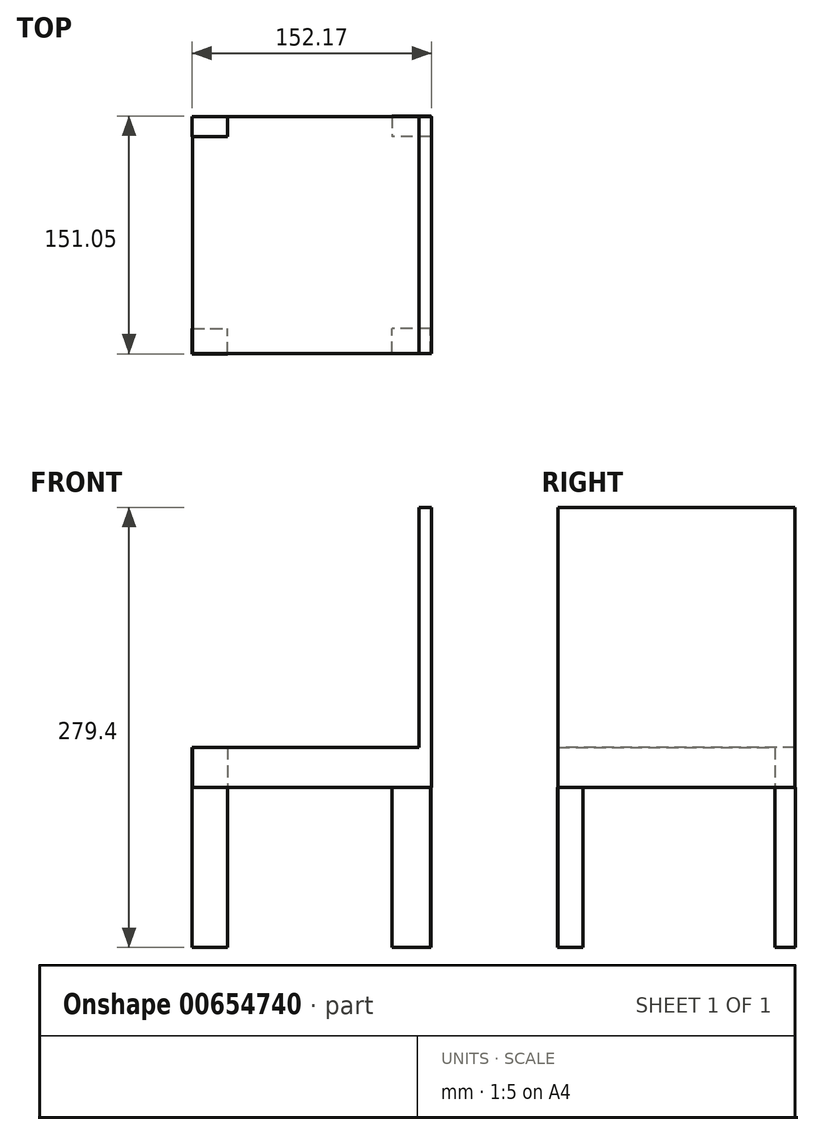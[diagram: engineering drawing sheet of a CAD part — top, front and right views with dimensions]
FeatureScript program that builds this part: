
annotation { "Feature Type Name" : "Feature", "Feature Type Description" : "" }
export const myFeature = defineFeature(function(context is Context, id is Id, definition is map)
    precondition{}
    {
        {
            var Q0;
            Q0=qCreatedBy(makeId("Top.planeOp"),FACE);
            var sketch = newSketch(context, id + "F0", { "sketchPlane" : qUnion([Q0])});
            skLineSegment(sketch, "E0.bottom", {"start": v(-76.1, -74.6) * mm, "end": v(-53.69, -74.6) * mm});
            skLineSegment(sketch, "E0.top", {"start": v(-76.1, -58.44) * mm, "end": v(-53.69, -58.44) * mm});
            skLineSegment(sketch, "E0.left", {"start": v(-76.1, -74.6) * mm, "end": v(-76.1, -58.44) * mm});
            skLineSegment(sketch, "E0.right", {"start": v(-53.69, -74.6) * mm, "end": v(-53.69, -58.44) * mm});
            skLineSegment(sketch, "E1.bottom", {"start": v(75.43, -74.27) * mm, "end": v(50.96, -74.27) * mm});
            skLineSegment(sketch, "E1.top", {"start": v(75.43, -58.44) * mm, "end": v(50.96, -58.44) * mm});
            skLineSegment(sketch, "E1.left", {"start": v(75.43, -74.27) * mm, "end": v(75.43, -58.44) * mm});
            skLineSegment(sketch, "E1.right", {"start": v(50.96, -74.27) * mm, "end": v(50.96, -58.44) * mm});
            skLineSegment(sketch, "E2.bottom", {"start": v(75.57, 76.45) * mm, "end": v(50.96, 76.45) * mm});
            skLineSegment(sketch, "E2.top", {"start": v(75.57, 63.39) * mm, "end": v(50.96, 63.39) * mm});
            skLineSegment(sketch, "E2.left", {"start": v(75.57, 76.45) * mm, "end": v(75.57, 63.39) * mm});
            skLineSegment(sketch, "E2.right", {"start": v(50.96, 76.45) * mm, "end": v(50.96, 63.39) * mm});
            skLineSegment(sketch, "E3.bottom", {"start": v(-75.96, 76.12) * mm, "end": v(-53.69, 76.12) * mm});
            skLineSegment(sketch, "E3.top", {"start": v(-75.96, 63.39) * mm, "end": v(-53.69, 63.39) * mm});
            skLineSegment(sketch, "E3.left", {"start": v(-75.96, 76.12) * mm, "end": v(-75.96, 63.39) * mm});
            skLineSegment(sketch, "E3.right", {"start": v(-53.69, 76.12) * mm, "end": v(-53.69, 63.39) * mm});
            skSolve(sketch);
        }
        {
            var Q0;
            Q0=makeQuery(id+"F0.imprint","IMPRINT",FACE,{"disambiguationData":[TD([[makeQuery(id+"F0.imprint","IMPRINT",EDGE,{"derivedFrom":sQuery(id+"F0.wireOp",EDGE,"E3.bottom")}),-1.0]])]});
            var Q1;
            Q1=makeQuery(id+"F0.imprint","IMPRINT",FACE,{"disambiguationData":[TD([[makeQuery(id+"F0.imprint","IMPRINT",EDGE,{"derivedFrom":sQuery(id+"F0.wireOp",EDGE,"E2.bottom")}),1.0]])]});
            var Q2;
            Q2=makeQuery(id+"F0.imprint","IMPRINT",FACE,{"disambiguationData":[TD([[makeQuery(id+"F0.imprint","IMPRINT",EDGE,{"derivedFrom":sQuery(id+"F0.wireOp",EDGE,"E1.bottom")}),-1.0]])]});
            var Q3;
            Q3=makeQuery(id+"F0.imprint","IMPRINT",FACE,{"disambiguationData":[TD([[makeQuery(id+"F0.imprint","IMPRINT",EDGE,{"derivedFrom":sQuery(id+"F0.wireOp",EDGE,"E0.bottom")}),1.0]])]});
            extrude(context, id + "F1", {"entities" : qUnion([Q0, Q1, Q2, Q3]), "depth" : 101.6 * mm, "offsetDistance" : 25.4 * mm});
        }
        {
            var Q0;
            Q0=makeQuery(id+"F1.opExtrude","CAP_FACE",FACE,{"disambiguationData":[OSD([sQuery(id+"F0.wireOp",EDGE,"E3.bottom"),sQuery(id+"F0.wireOp",EDGE,"E3.top"),sQuery(id+"F0.wireOp",EDGE,"E3.left"),sQuery(id+"F0.wireOp",EDGE,"E3.right")])],"isStart":false});
            var sketch = newSketch(context, id + "F2", { "sketchPlane" : qUnion([Q0])});
            skLineSegment(sketch, "E4.bottom", {"start": v(-75.77, -74.44) * mm, "end": v(76.07, -74.44) * mm});
            skLineSegment(sketch, "E4.top", {"start": v(-75.77, 76.2) * mm, "end": v(76.07, 76.2) * mm});
            skLineSegment(sketch, "E4.left", {"start": v(-75.77, -74.44) * mm, "end": v(-75.77, 76.2) * mm});
            skLineSegment(sketch, "E4.right", {"start": v(76.07, -74.44) * mm, "end": v(76.07, 76.2) * mm});
            skSolve(sketch);
        }
        {
            var Q0;
            {var subQ4=sQuery(id+"F2.wireOp",EDGE,"E4.bottom");Q0=makeQuery(id+"F2.imprint","IMPRINT",FACE,{"disambiguationData":[TD([[makeQuery(id+"F2.imprint","IMPRINT",EDGE,{"derivedFrom":subQ4}),1.0]])]});}
            extrude(context, id + "F3", {"entities" : qUnion([Q0]), "depth" : 25.4 * mm, "offsetDistance" : 25.4 * mm});
        }
        {
            var Q0;
            Q0=makeQuery(id+"F1.opExtrude","CAP_FACE",FACE,{"disambiguationData":[OSD([sQuery(id+"F0.wireOp",EDGE,"E3.bottom"),sQuery(id+"F0.wireOp",EDGE,"E3.top"),sQuery(id+"F0.wireOp",EDGE,"E3.left"),sQuery(id+"F0.wireOp",EDGE,"E3.right")])],"isStart":false});
            var sketch = newSketch(context, id + "F4", { "sketchPlane" : qUnion([Q0])});
            skLineSegment(sketch, "E5.bottom", {"start": v(-75.96, 76.12) * mm, "end": v(-53.69, 76.12) * mm});
            skLineSegment(sketch, "E5.top", {"start": v(-75.96, 63.39) * mm, "end": v(-53.69, 63.39) * mm});
            skLineSegment(sketch, "E5.left", {"start": v(-75.96, 76.12) * mm, "end": v(-75.96, 63.39) * mm});
            skLineSegment(sketch, "E5.right", {"start": v(-53.69, 76.12) * mm, "end": v(-53.69, 63.39) * mm});
            skSolve(sketch);
        }
        {
            var Q0;
            Q0=makeQuery(id+"F4.imprint","IMPRINT",FACE,{"disambiguationData":[TD([[makeQuery(id+"F4.imprint","IMPRINT",EDGE,{"derivedFrom":sQuery(id+"F4.wireOp",EDGE,"E5.bottom")}),-1.0]])]});
            extrude(context, id + "F5", {"entities" : qUnion([Q0]), "depth" : 25.4 * mm, "offsetDistance" : 25.4 * mm});
        }
        {
            var Q0;
            Q0=makeQuery(id+"F3.opExtrude","CAP_FACE",FACE,{"disambiguationData":[OSD([sQuery(id+"F0.wireOp",EDGE,"E3.bottom"),sQuery(id+"F0.wireOp",EDGE,"E3.top"),sQuery(id+"F0.wireOp",EDGE,"E3.right"),sQuery(id+"F2.wireOp",EDGE,"E4.bottom"),sQuery(id+"F2.wireOp",EDGE,"E4.top"),sQuery(id+"F2.wireOp",EDGE,"E4.left"),sQuery(id+"F2.wireOp",EDGE,"E4.right")])],"isStart":false});
            var sketch = newSketch(context, id + "F6", { "sketchPlane" : qUnion([Q0])});
            skLineSegment(sketch, "E6.bottom", {"start": v(76.07, 76.2) * mm, "end": v(67.94, 76.2) * mm});
            skLineSegment(sketch, "E6.top", {"start": v(76.07, -74.44) * mm, "end": v(67.94, -74.44) * mm});
            skLineSegment(sketch, "E6.left", {"start": v(76.07, 76.2) * mm, "end": v(76.07, -74.44) * mm});
            skLineSegment(sketch, "E6.right", {"start": v(67.94, 76.2) * mm, "end": v(67.94, -74.44) * mm});
            skSolve(sketch);
        }
        {
            var Q0;
            Q0=makeQuery(id+"F6.imprint","IMPRINT",FACE,{"disambiguationData":[TD([[makeQuery(id+"F6.imprint","IMPRINT",EDGE,{"derivedFrom":sQuery(id+"F6.wireOp",EDGE,"E6.bottom")}),-1.0]])]});
            extrude(context, id + "F7", {"entities" : qUnion([Q0]), "operationType" : NewBodyOperationType.ADD, "depth" : 76.2 * mm, "offsetDistance" : 25.4 * mm});
        }
        {
            var Q0;
            Q0=makeQuery(id+"F7.opExtrude","CAP_FACE",FACE,{"disambiguationData":[OSD([sQuery(id+"F6.wireOp",EDGE,"E6.bottom"),sQuery(id+"F6.wireOp",EDGE,"E6.top"),sQuery(id+"F6.wireOp",EDGE,"E6.left"),sQuery(id+"F6.wireOp",EDGE,"E6.right")])],"isStart":false});
            extrude(context, id + "F8", {"entities" : qUnion([Q0]), "operationType" : NewBodyOperationType.ADD, "depth" : 152.4 * mm, "offsetDistance" : 25.4 * mm});
        }
        {
            var Q0;
            Q0=makeQuery(id+"F8.opExtrude","CAP_FACE",FACE,{"disambiguationData":[OSD([sQuery(id+"F6.wireOp",EDGE,"E6.bottom"),sQuery(id+"F6.wireOp",EDGE,"E6.top"),sQuery(id+"F6.wireOp",EDGE,"E6.left"),sQuery(id+"F6.wireOp",EDGE,"E6.right")])],"isStart":false});
            extrude(context, id + "F9", {"entities" : qUnion([Q0]), "operationType" : NewBodyOperationType.ADD, "depth" : 127 * mm, "offsetDistance" : 25.4 * mm});
        }
        {
            var Q0;
            Q0=makeQuery(id+"F9.opExtrude","CAP_FACE",FACE,{"disambiguationData":[OSD([sQuery(id+"F6.wireOp",EDGE,"E6.bottom"),sQuery(id+"F6.wireOp",EDGE,"E6.top"),sQuery(id+"F6.wireOp",EDGE,"E6.left"),sQuery(id+"F6.wireOp",EDGE,"E6.right")])],"isStart":false});
            extrude(context, id + "F10", {"entities" : qUnion([Q0]), "operationType" : NewBodyOperationType.ADD, "depth" : 25.4 * mm, "offsetDistance" : 25.4 * mm});
        }
        {
            var Q0;
            Q0=makeQuery(id+"F10.opExtrude","CAP_FACE",FACE,{"disambiguationData":[OSD([sQuery(id+"F6.wireOp",EDGE,"E6.bottom"),sQuery(id+"F6.wireOp",EDGE,"E6.top"),sQuery(id+"F6.wireOp",EDGE,"E6.left"),sQuery(id+"F6.wireOp",EDGE,"E6.right")])],"isStart":false});
            extrude(context, id + "F11", {"entities" : qUnion([Q0]), "operationType" : NewBodyOperationType.REMOVE, "oppositeDirection" : true, "depth" : 76.2 * mm, "offsetDistance" : 25.4 * mm});
        }
        {
            var Q0;
            Q0=makeQuery(id+"F11.boolean.opBoolean","COPY",FACE,{"derivedFrom":makeQuery(id+"F11.opExtrude","CAP_FACE",FACE,{"disambiguationData":[OSD([sQuery(id+"F6.wireOp",EDGE,"E6.bottom"),sQuery(id+"F6.wireOp",EDGE,"E6.top"),sQuery(id+"F6.wireOp",EDGE,"E6.left"),sQuery(id+"F6.wireOp",EDGE,"E6.right")])],"isStart":false})});
            extrude(context, id + "F12", {"entities" : qUnion([Q0]), "operationType" : NewBodyOperationType.REMOVE, "oppositeDirection" : true, "depth" : 76.2 * mm, "offsetDistance" : 25.4 * mm});
        }
        {
            var Q0;
            Q0=makeQuery(id+"F12.boolean.opBoolean","COPY",FACE,{"derivedFrom":makeQuery(id+"F12.opExtrude","CAP_FACE",FACE,{"disambiguationData":[OSD([sQuery(id+"F6.wireOp",EDGE,"E6.bottom"),sQuery(id+"F6.wireOp",EDGE,"E6.top"),sQuery(id+"F6.wireOp",EDGE,"E6.left"),sQuery(id+"F6.wireOp",EDGE,"E6.right")])],"isStart":false})});
            extrude(context, id + "F13", {"entities" : qUnion([Q0]), "operationType" : NewBodyOperationType.REMOVE, "oppositeDirection" : true, "depth" : 76.2 * mm, "offsetDistance" : 25.4 * mm});
        }
    });
